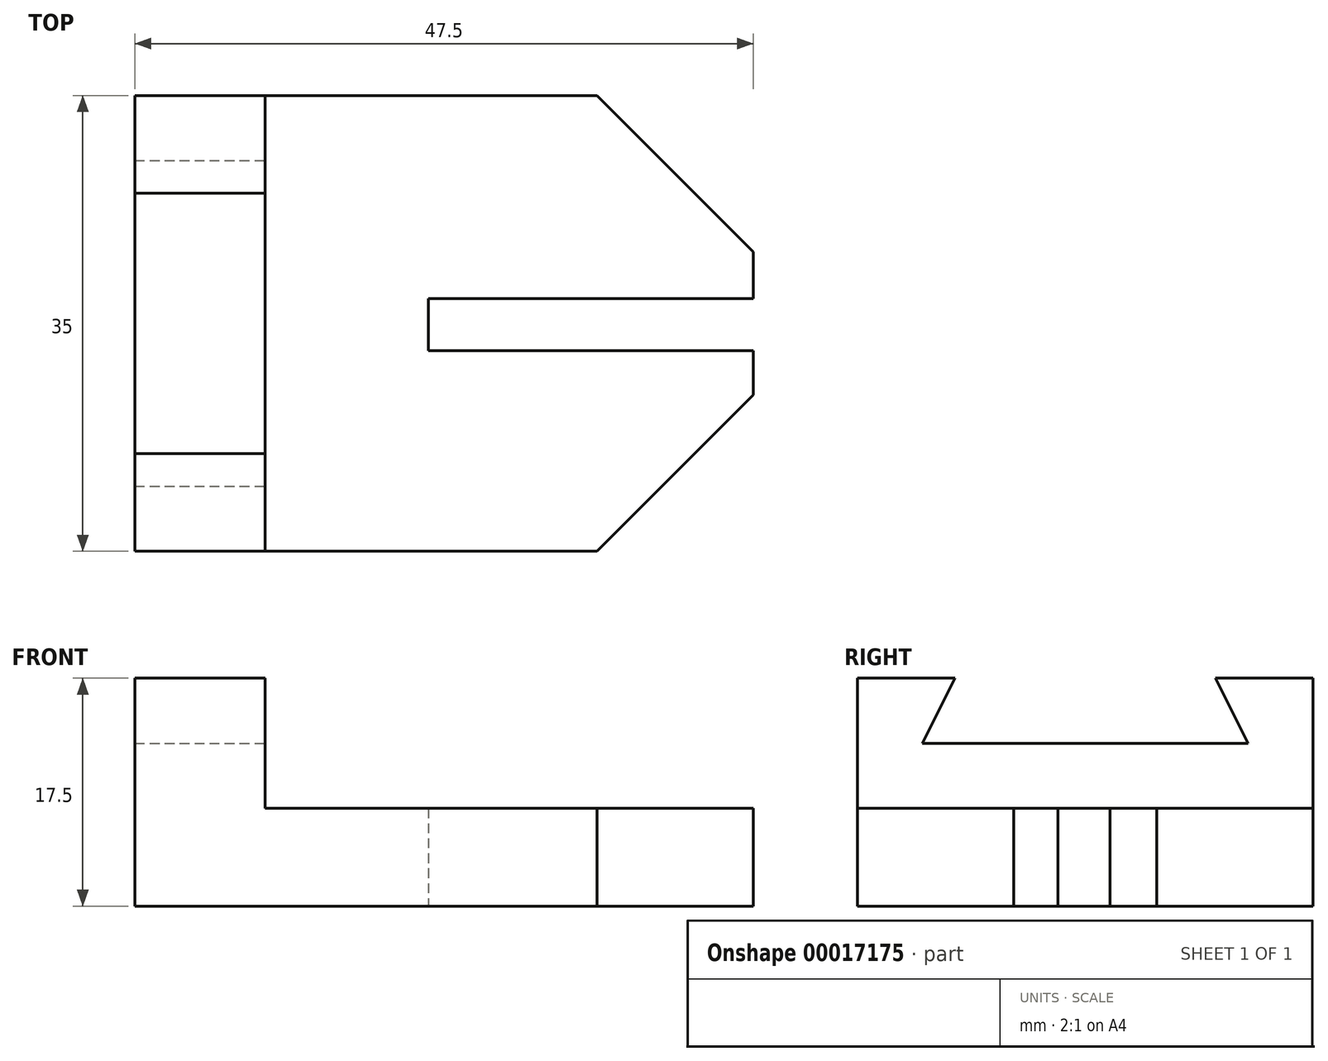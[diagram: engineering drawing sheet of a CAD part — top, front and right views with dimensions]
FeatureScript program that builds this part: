
annotation { "Feature Type Name" : "Feature", "Feature Type Description" : "" }
export const myFeature = defineFeature(function(context is Context, id is Id, definition is map)
    precondition{}
    {
        {
            var Q0;
            Q0=qCreatedBy(makeId("Top.planeOp"),FACE);
            var sketch = newSketch(context, id + "F0", { "sketchPlane" : qUnion([Q0])});
            skLineSegment(sketch, "E0.rect.right", {"start": v(-40.15, 20.04) * mm, "end": v(-40.15, 55.04) * mm});
            skLineSegment(sketch, "E1", {"start": v(-40.15, 55.04) * mm, "end": v(-2.65, 55.04) * mm});
            skLineSegment(sketch, "E2", {"start": v(-2.65, 20.04) * mm, "end": v(-40.15, 20.04) * mm});
            skLineSegment(sketch, "E3", {"start": v(-40.15, 55.04) * mm, "end": v(-50.15, 55.04) * mm});
            skLineSegment(sketch, "E4", {"start": v(-50.15, 55.04) * mm, "end": v(-50.15, 20.04) * mm});
            skLineSegment(sketch, "E5", {"start": v(-50.15, 20.04) * mm, "end": v(-40.15, 20.04) * mm});
            skLineSegment(sketch, "E6", {"start": v(-2.65, 55.04) * mm, "end": v(-2.65, 42.04) * mm});
            skLineSegment(sketch, "E7", {"start": v(-2.65, 20.04) * mm, "end": v(-2.65, 33.04) * mm});
            skLineSegment(sketch, "E8", {"start": v(-2.65, 42.04) * mm, "end": v(-2.65, 33.04) * mm});
            skLineSegment(sketch, "E9.bottom", {"start": v(-27.6, 39.45) * mm, "end": v(-2.6, 39.45) * mm});
            skLineSegment(sketch, "E9.top", {"start": v(-27.6, 35.45) * mm, "end": v(-2.6, 35.45) * mm});
            skLineSegment(sketch, "E9.left", {"start": v(-27.6, 39.45) * mm, "end": v(-27.6, 35.45) * mm});
            skLineSegment(sketch, "E9.right", {"start": v(-2.6, 39.45) * mm, "end": v(-2.6, 35.45) * mm});
            skSolve(sketch);
        }
        {
            var Q0;
            Q0=makeQuery(id+"F0.imprint","IMPRINT",FACE,{"disambiguationData":[TD([[makeQuery(id+"F0.imprint","IMPRINT",EDGE,{"derivedFrom":sQuery(id+"F0.wireOp",EDGE,"E0.rect.right")}),-1.0]])]});
            extrude(context, id + "F1", {"entities" : qUnion([Q0]), "depth" : 7.5 * mm});
        }
        {
            var Q0;
            Q0=makeQuery(id+"F0.imprint","IMPRINT",FACE,{"disambiguationData":[TD([[makeQuery(id+"F0.imprint","IMPRINT",EDGE,{"derivedFrom":sQuery(id+"F0.wireOp",EDGE,"E0.rect.right")}),1.0]])]});
            extrude(context, id + "F2", {"entities" : qUnion([Q0]), "operationType" : NewBodyOperationType.ADD, "depth" : 17.5 * mm});
        }
        {
            var Q0;
            Q0=makeQuery(id+"F1.opExtrude","SWEPT_EDGE",EDGE,{"disambiguationData":[OSD([sQuery(id+"F0.wireOp",EDGE,"E2"),sQuery(id+"F0.wireOp",EDGE,"E7")])]});
            chamfer(context, id + "F3", {"entities" : qUnion([Q0]), "width" : 12 * mm, "tangentPropagation" : true});
        }
        {
            var Q0;
            Q0=makeQuery(id+"F1.opExtrude","SWEPT_EDGE",EDGE,{"disambiguationData":[OSD([sQuery(id+"F0.wireOp",EDGE,"E1"),sQuery(id+"F0.wireOp",EDGE,"E6")])]});
            chamfer(context, id + "F4", {"entities" : qUnion([Q0]), "width" : 12 * mm, "tangentPropagation" : true});
        }
        {
            var Q0;
            Q0=makeQuery(id+"F2.opExtrude","SWEPT_FACE",FACE,{"disambiguationData":[OSD([sQuery(id+"F0.wireOp",EDGE,"E0.rect.right")])]});
            var sketch = newSketch(context, id + "F5", { "sketchPlane" : qUnion([Q0])});
            skPoint(sketch, "E10", {"position": v(27.54, 17.5) * mm});
            skPoint(sketch, "E11", {"position": v(47.54, 17.5) * mm});
            skPoint(sketch, "E12", {"position": v(50.04, 12.5) * mm});
            skPoint(sketch, "E13", {"position": v(25.04, 12.5) * mm});
            skLineSegment(sketch, "E14", {"start": v(25.04, 12.5) * mm, "end": v(25.04, 17.5) * mm});
            skLineSegment(sketch, "E15", {"start": v(50.14, 17.5) * mm, "end": v(50.04, 12.5) * mm});
            skLineSegment(sketch, "E16", {"start": v(47.54, 17.5) * mm, "end": v(50.04, 12.5) * mm});
            skLineSegment(sketch, "E17", {"start": v(25.04, 12.5) * mm, "end": v(27.54, 17.5) * mm});
            skLineSegment(sketch, "E18", {"start": v(27.54, 17.5) * mm, "end": v(47.54, 17.5) * mm});
            skLineSegment(sketch, "E19", {"start": v(50.04, 12.5) * mm, "end": v(25.04, 12.5) * mm});
            skSolve(sketch);
        }
        {
            var Q0;
            Q0=makeQuery(id+"F5.imprint","IMPRINT",FACE,{"disambiguationData":[TD([[makeQuery(id+"F5.imprint","IMPRINT",EDGE,{"derivedFrom":sQuery(id+"F5.wireOp",EDGE,"E16")}),-1.0]])]});
            extrude(context, id + "F6", {"entities" : qUnion([Q0]), "operationType" : NewBodyOperationType.REMOVE, "oppositeDirection" : true, "depth" : 25 * mm});
        }
    });
